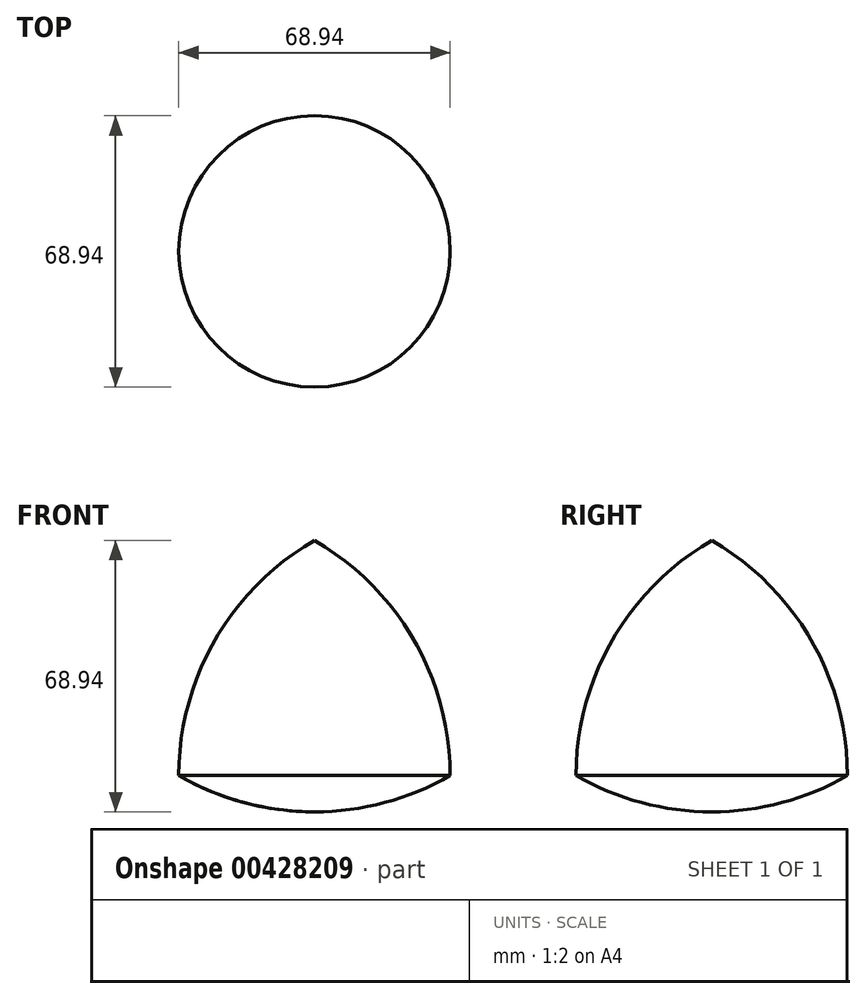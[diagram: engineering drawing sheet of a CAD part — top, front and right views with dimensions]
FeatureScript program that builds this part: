
annotation { "Feature Type Name" : "Feature", "Feature Type Description" : "" }
export const myFeature = defineFeature(function(context is Context, id is Id, definition is map)
    precondition{}
    {
        {
            var Q0;
            Q0=qCreatedBy(makeId("Front.planeOp"),FACE);
            var sketch = newSketch(context, id + "F0", { "sketchPlane" : qUnion([Q0])});
            skCircle(sketch, "E0.cCircle", {"center": v(0, 0) * mm, "radius": 39.8 * mm, "construction": true});
            skLineSegment(sketch, "E0.0", {"start": v(0, 39.8) * mm, "end": v(34.47, -19.9) * mm});
            skLineSegment(sketch, "E0.1", {"start": v(34.47, -19.9) * mm, "end": v(-34.47, -19.9) * mm});
            skLineSegment(sketch, "E0.2", {"start": v(-34.47, -19.9) * mm, "end": v(0, 39.8) * mm});
            skArc(sketch, "E1", {"start": v(0, 39.8) * mm, "mid": v(25.23, 14.57) * mm, "end": v(34.47, -19.9) * mm});
            skArc(sketch, "E2", {"start": v(-34.47, -19.9) * mm, "mid": v(-25.23, 14.57) * mm, "end": v(0, 39.8) * mm});
            skArc(sketch, "E3", {"start": v(34.47, -19.9) * mm, "mid": v(0, -29.14) * mm, "end": v(-34.47, -19.9) * mm});
            skLineSegment(sketch, "E4", {"start": v(0, 39.8) * mm, "end": v(0, -29.14) * mm});
            skSolve(sketch);
        }
        {
            var Q0;
            Q0=makeQuery(id+"F0.imprint","IMPRINT",FACE,{"disambiguationData":[TD([[makeQuery(id+"F0.imprint","IMPRINT",EDGE,{"derivedFrom":sQuery(id+"F0.wireOp",EDGE,"E0.2")}),1.0]])]});
            var Q1;
            {var subQ1=sQuery(id+"F0.wireOp",EDGE,"E0.2");Q1=makeQuery(id+"F0.imprint","IMPRINT",FACE,{"disambiguationData":[TD([[makeQuery(id+"F0.imprint","IMPRINT",EDGE,{"derivedFrom":subQ1}),-1.0]])]});}
            var Q2;
            {var subQ0=sQuery(id+"F0.wireOp",EDGE,"E3");var subQ3=sQuery(id+"F0.wireOp",EDGE,"E4");var subQ5=makeQuery(id+"F0.imprint","INTERSECT",VERTEX,{"derivedFrom":[subQ0,subQ3]});Q2=makeQuery(id+"F0.imprint","IMPRINT",FACE,{"disambiguationData":[TD([[makeQuery(id+"F0.imprint","IMPRINT",EDGE,{"disambiguationData":[TD([[subQ5,1.0]])],"derivedFrom":subQ3}),-1.0]])]});}
            var Q3;
            Q3=sQuery(id+"F0.wireOp",EDGE,"E4");
            revolve(context, id + "F1", {"entities" : qUnion([Q0, Q1, Q2]), "axis" : qUnion([Q3]), "revolveType" : RevolveType.FULL});
        }
    });
